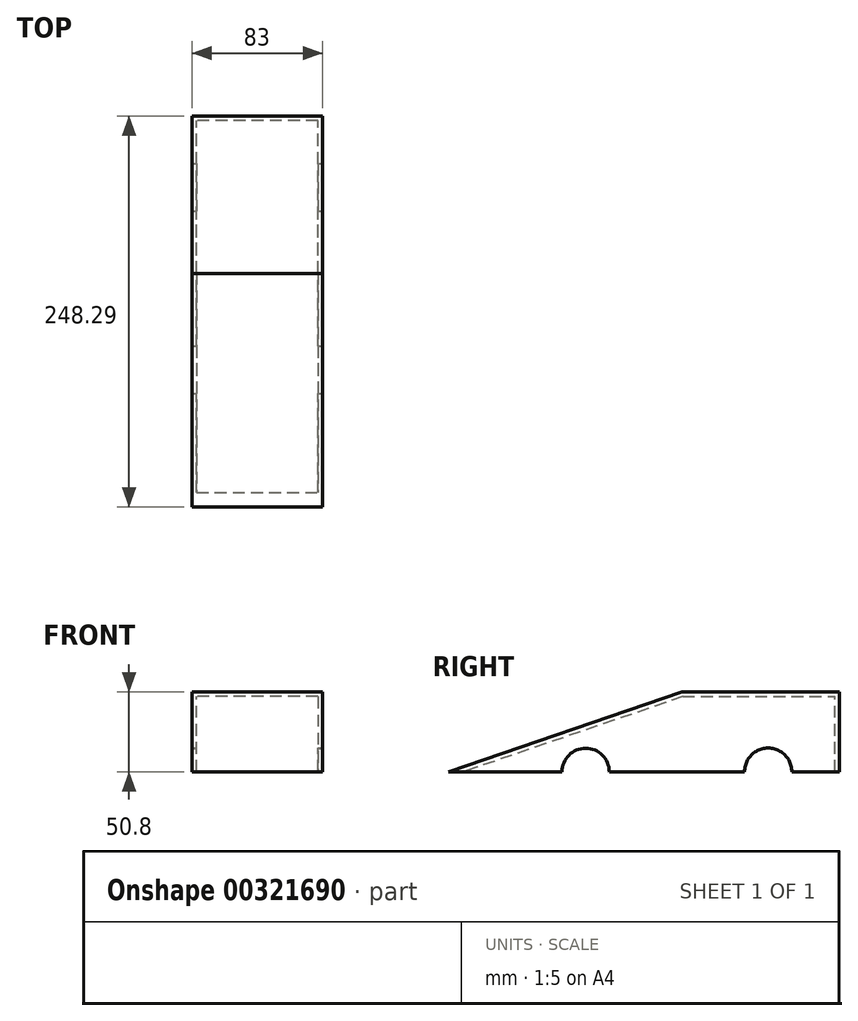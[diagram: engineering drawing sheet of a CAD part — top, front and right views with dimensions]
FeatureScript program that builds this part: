
annotation { "Feature Type Name" : "Feature", "Feature Type Description" : "" }
export const myFeature = defineFeature(function(context is Context, id is Id, definition is map)
    precondition{}
    {
        {
            var Q0;
            Q0=qCreatedBy(makeId("Right.planeOp"),FACE);
            var sketch = newSketch(context, id + "F0", { "sketchPlane" : qUnion([Q0])});
            skLineSegment(sketch, "E0.bottom", {"start": v(-100, -25.4) * mm, "end": v(100, -25.4) * mm});
            skLineSegment(sketch, "E0.top", {"start": v(-100, 25.4) * mm, "end": v(100, 25.4) * mm});
            skLineSegment(sketch, "E0.left", {"start": v(-100, -25.4) * mm, "end": v(-100, 25.4) * mm});
            skLineSegment(sketch, "E0.right", {"start": v(100, -25.4) * mm, "end": v(100, 25.4) * mm});
            skPoint(sketch, "E0.middle", {"position": v(0, 0) * mm});
            skSolve(sketch);
        }
        {
            var Q0;
            Q0=makeQuery(id+"F0.imprint","IMPRINT",FACE,{"disambiguationData":[TD([[makeQuery(id+"F0.imprint","IMPRINT",EDGE,{"derivedFrom":sQuery(id+"F0.wireOp",EDGE,"E0.bottom")}),1.0]])]});
            extrude(context, id + "F1", {"entities" : qUnion([Q0]), "depth" : 83 * mm});
        }
        {
            var Q0;
            Q0=makeQuery(id+"F1.opExtrude","CAP_FACE",FACE,{"disambiguationData":[OSD([sQuery(id+"F0.wireOp",EDGE,"E0.bottom"),sQuery(id+"F0.wireOp",EDGE,"E0.top"),sQuery(id+"F0.wireOp",EDGE,"E0.left"),sQuery(id+"F0.wireOp",EDGE,"E0.right")])],"isStart":false});
            var sketch = newSketch(context, id + "F2", { "sketchPlane" : qUnion([Q0])});
            skLineSegment(sketch, "E1", {"start": v(0, 25.4) * mm, "end": v(-148.3, -25.4) * mm});
            skLineSegment(sketch, "E2", {"start": v(-148.3, -25.4) * mm, "end": v(0, -25.4) * mm});
            skLineSegment(sketch, "E3", {"start": v(0, -25.4) * mm, "end": v(0, 25.4) * mm});
            skSolve(sketch);
        }
        {
            var Q0;
            {var subQ1=makeQuery(id+"F1.opExtrude","CAP_EDGE",EDGE,{"disambiguationData":[OSD([sQuery(id+"F0.wireOp",EDGE,"E0.top")])],"isStart":false});var subQ3=makeQuery(id+"F1.opExtrude","CAP_EDGE",EDGE,{"disambiguationData":[OSD([sQuery(id+"F0.wireOp",EDGE,"E0.left")])],"isStart":false});var subQ5=makeQuery(id+"F2.imprint","INTERSECT",VERTEX,{"derivedFrom":[subQ1,subQ3]});Q0=makeQuery(id+"F2.imprint","IMPRINT",FACE,{"disambiguationData":[TD([[makeQuery(id+"F2.imprint","IMPRINT",EDGE,{"disambiguationData":[TD([[subQ5,1.0]])],"derivedFrom":subQ3}),-1.0]])]});}
            extrude(context, id + "F3", {"entities" : qUnion([Q0]), "operationType" : NewBodyOperationType.REMOVE, "oppositeDirection" : true, "depth" : 83 * mm});
        }
        {
            var Q0;
            Q0 = qSketchRegion(id + "F2", true);
            extrude(context, id + "F4", {"entities" : qUnion([Q0]), "operationType" : NewBodyOperationType.ADD, "oppositeDirection" : true, "depth" : 83 * mm});
        }
        {
            var Q0;
            Q0=makeQuery(id+"F4.boolean.opBoolean","MERGE",FACE,{"derivedFrom":[makeQuery(id+"F1.opExtrude","SWEPT_FACE",FACE,{"disambiguationData":[OSD([sQuery(id+"F0.wireOp",EDGE,"E0.bottom")])]}),makeQuery(id+"F4.opExtrude","SWEPT_FACE",FACE,{"disambiguationData":[OSD([sQuery(id+"F2.wireOp",EDGE,"E2")])]})]});
            shell(context, id + "F5", {"entities" : qUnion([Q0]), "thickness" : 3 * mm});
        }
        {
            var Q0;
            Q0=makeQuery(id+"F4.boolean.opBoolean","MERGE",FACE,{"derivedFrom":[makeQuery(id+"F1.opExtrude","CAP_FACE",FACE,{"disambiguationData":[OSD([sQuery(id+"F0.wireOp",EDGE,"E0.bottom"),sQuery(id+"F0.wireOp",EDGE,"E0.top"),sQuery(id+"F0.wireOp",EDGE,"E0.left"),sQuery(id+"F0.wireOp",EDGE,"E0.right")])],"isStart":false}),makeQuery(id+"F4.opExtrude","CAP_FACE",FACE,{"disambiguationData":[OSD([sQuery(id+"F2.wireOp",EDGE,"E1"),sQuery(id+"F2.wireOp",EDGE,"E2"),sQuery(id+"F2.wireOp",EDGE,"E3")])],"isStart":true})]});
            var sketch = newSketch(context, id + "F6", { "sketchPlane" : qUnion([Q0])});
            skArc(sketch, "E4", {"start": v(-46.23, -25.4) * mm, "mid": v(-61.23, -10.4) * mm, "end": v(-76.23, -25.4) * mm});
            skArc(sketch, "E5", {"start": v(69.7, -25.4) * mm, "mid": v(54.7, -10.22) * mm, "end": v(39.7, -25.4) * mm});
            skSolve(sketch);
        }
        {
            var Q0;
            {var subQ0=sQuery(id+"F6.wireOp",EDGE,"E4");Q0=makeQuery(id+"F6.imprint","IMPRINT",FACE,{"disambiguationData":[TD([[makeQuery(id+"F6.imprint","IMPRINT",EDGE,{"derivedFrom":subQ0}),1.0]])]});}
            var Q1;
            {var subQ0=sQuery(id+"F6.wireOp",EDGE,"E5");Q1=makeQuery(id+"F6.imprint","IMPRINT",FACE,{"disambiguationData":[TD([[makeQuery(id+"F6.imprint","IMPRINT",EDGE,{"derivedFrom":subQ0}),1.0]])]});}
            extrude(context, id + "F7", {"entities" : qUnion([Q0, Q1]), "operationType" : NewBodyOperationType.REMOVE, "oppositeDirection" : true, "depth" : 101.6 * mm});
        }
    });
